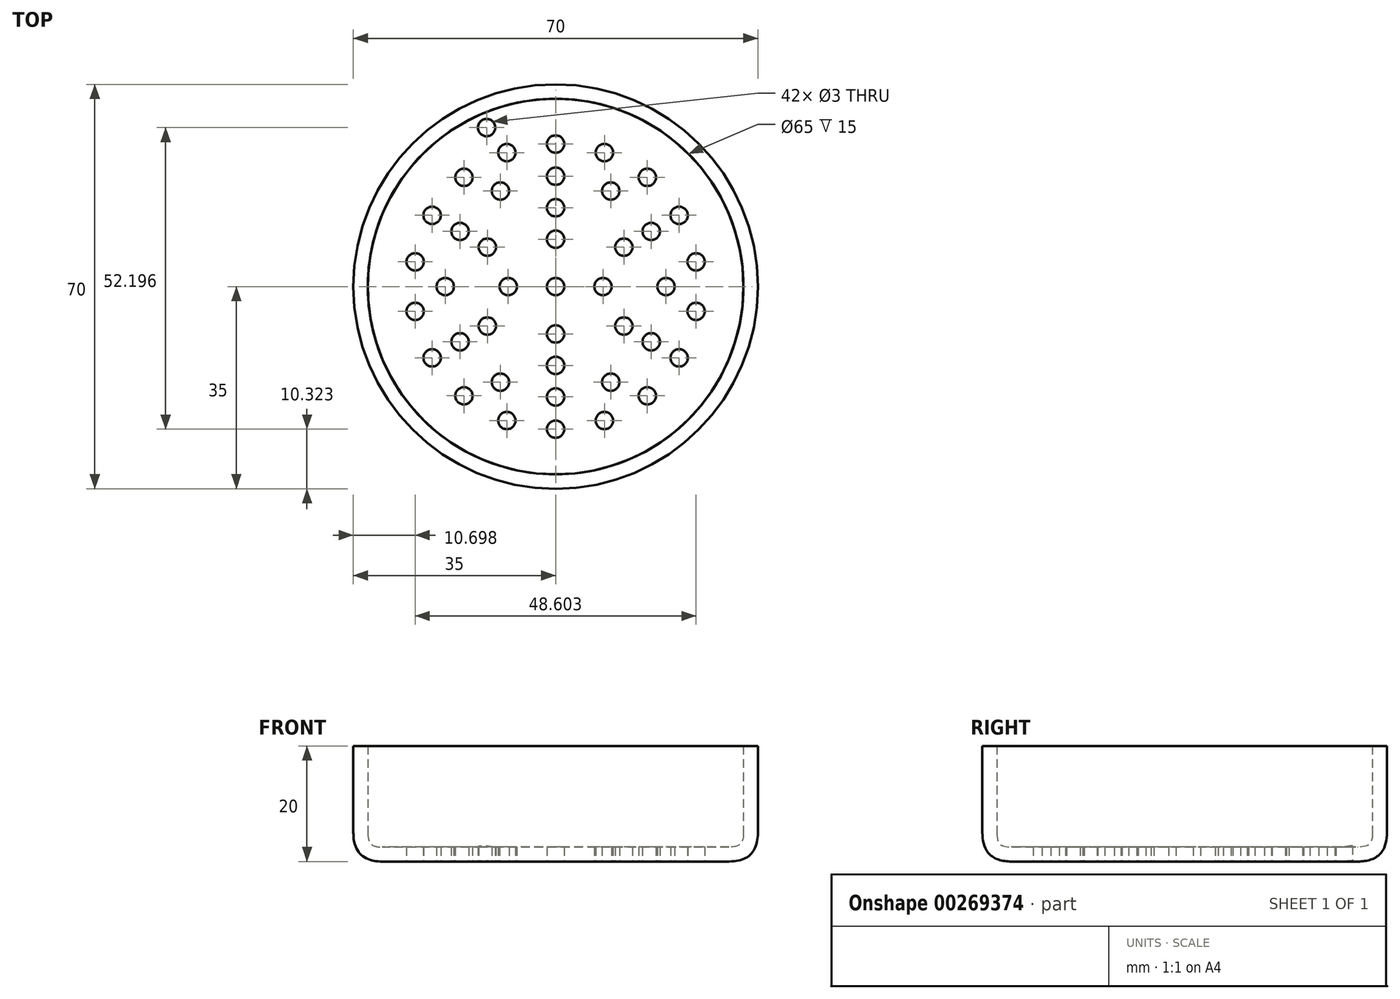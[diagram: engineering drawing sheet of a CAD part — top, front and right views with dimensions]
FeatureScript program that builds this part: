
annotation { "Feature Type Name" : "Feature", "Feature Type Description" : "" }
export const myFeature = defineFeature(function(context is Context, id is Id, definition is map)
    precondition{}
    {
        {
            var Q0;
            Q0=qCreatedBy(makeId("Top.planeOp"),FACE);
            var sketch = newSketch(context, id + "F0", { "sketchPlane" : qUnion([Q0])});
            skCircle(sketch, "E0", {"center": v(0, 0) * mm, "radius": 35 * mm});
            skSolve(sketch);
        }
        {
            var Q0;
            Q0=makeQuery(id+"F0.imprint","IMPRINT",FACE,{"disambiguationData":[TD([[makeQuery(id+"F0.imprint","IMPRINT",EDGE,{"derivedFrom":sQuery(id+"F0.wireOp",EDGE,"E0")}),1.0]])]});
            extrude(context, id + "F1", {"entities" : qUnion([Q0]), "depth" : 20 * mm});
        }
        {
            var Q0;
            Q0=makeQuery(id+"F1.opExtrude","CAP_EDGE",EDGE,{"disambiguationData":[OSD([sQuery(id+"F0.wireOp",EDGE,"E0")])],"isStart":true});
            fillet(context, id + "F2", {"entities" : qUnion([Q0]), "radius" : 5 * mm, "tangentPropagation" : true, "rho" : 0.5, "crossSection" : FilletCrossSection.CONIC, "allowEdgeOverflow" : false});
        }
        {
            var Q0;
            Q0=makeQuery(id+"F1.opExtrude","CAP_FACE",FACE,{"disambiguationData":[OSD([sQuery(id+"F0.wireOp",EDGE,"E0")])],"isStart":false});
            shell(context, id + "F3", {"entities" : qUnion([Q0]), "thickness" : 2.5 * mm});
        }
        {
            var Q0;
            Q0=makeQuery(id+"F1.opExtrude","CAP_FACE",FACE,{"disambiguationData":[OSD([sQuery(id+"F0.wireOp",EDGE,"E0")])],"isStart":true});
            var sketch = newSketch(context, id + "F4", { "sketchPlane" : qUnion([Q0])});
            skPoint(sketch, "E1", {"position": v(0, 0) * mm});
            skPoint(sketch, "E2", {"position": v(3.96, -29.74) * mm});
            skPoint(sketch, "E3", {"position": v(-11.94, -27.52) * mm});
            skPoint(sketch, "E4", {"position": v(0, -19.1) * mm});
            skPoint(sketch, "E5", {"position": v(-30, 0) * mm});
            skPoint(sketch, "E6", {"position": v(0, -8.2) * mm});
            skPoint(sketch, "E7", {"position": v(-33.56, -2.34) * mm});
            skPoint(sketch, "E8", {"position": v(-4.38, -20.96) * mm});
            skPoint(sketch, "E9", {"position": v(0, -13.64) * mm});
            skPoint(sketch, "E10", {"position": v(-12.69, -12.92) * mm});
            skPoint(sketch, "E11", {"position": v(0, -24.68) * mm});
            skPoint(sketch, "E12", {"position": v(-4.38, -46.93) * mm});
            skPoint(sketch, "E13.1.0", {"position": v(7.1, 4.1) * mm});
            skPoint(sketch, "E13.2.0", {"position": v(-7.1, 4.1) * mm});
            skPoint(sketch, "E14.1.0", {"position": v(8.2, 0) * mm});
            skPoint(sketch, "E14.2.0", {"position": v(0, 8.2) * mm});
            skPoint(sketch, "E14.3.0", {"position": v(-8.2, 0) * mm});
            skPoint(sketch, "E15.1.0", {"position": v(11.81, -6.82) * mm});
            skPoint(sketch, "E15.2.0", {"position": v(11.81, 6.82) * mm});
            skPoint(sketch, "E15.3.0", {"position": v(0, 13.64) * mm});
            skPoint(sketch, "E15.4.0", {"position": v(-11.81, 6.82) * mm});
            skPoint(sketch, "E15.5.0", {"position": v(-11.81, -6.82) * mm});
            skPoint(sketch, "E16.1.0", {"position": v(9.55, -16.54) * mm});
            skPoint(sketch, "E16.2.0", {"position": v(16.54, -9.55) * mm});
            skPoint(sketch, "E16.3.0", {"position": v(19.1, 0) * mm});
            skPoint(sketch, "E16.4.0", {"position": v(16.54, 9.55) * mm});
            skPoint(sketch, "E16.5.0", {"position": v(9.55, 16.54) * mm});
            skPoint(sketch, "E16.6.0", {"position": v(0, 19.1) * mm});
            skPoint(sketch, "E16.7.0", {"position": v(-9.55, 16.54) * mm});
            skPoint(sketch, "E16.8.0", {"position": v(-16.54, 9.55) * mm});
            skPoint(sketch, "E16.9.0", {"position": v(-19.1, 0) * mm});
            skPoint(sketch, "E16.10.0", {"position": v(-16.54, -9.55) * mm});
            skPoint(sketch, "E16.11.0", {"position": v(-9.55, -16.54) * mm});
            skPoint(sketch, "E17.1.0", {"position": v(8.44, -23.19) * mm});
            skPoint(sketch, "E17.2.0", {"position": v(15.86, -18.9) * mm});
            skPoint(sketch, "E17.3.0", {"position": v(21.37, -12.34) * mm});
            skPoint(sketch, "E17.4.0", {"position": v(24.3, -4.29) * mm});
            skPoint(sketch, "E17.5.0", {"position": v(24.3, 4.29) * mm});
            skPoint(sketch, "E17.6.0", {"position": v(21.37, 12.34) * mm});
            skPoint(sketch, "E17.7.0", {"position": v(15.86, 18.9) * mm});
            skPoint(sketch, "E17.8.0", {"position": v(8.44, 23.19) * mm});
            skPoint(sketch, "E17.9.0", {"position": v(0, 24.68) * mm});
            skPoint(sketch, "E17.10.0", {"position": v(-8.44, 23.19) * mm});
            skPoint(sketch, "E17.11.0", {"position": v(-15.86, 18.9) * mm});
            skPoint(sketch, "E17.12.0", {"position": v(-21.37, 12.34) * mm});
            skPoint(sketch, "E17.13.0", {"position": v(-24.3, 4.29) * mm});
            skPoint(sketch, "E17.14.0", {"position": v(-24.3, -4.29) * mm});
            skPoint(sketch, "E17.15.0", {"position": v(-21.37, -12.34) * mm});
            skPoint(sketch, "E17.16.0", {"position": v(-15.86, -18.9) * mm});
            skPoint(sketch, "E17.17.0", {"position": v(-8.44, -23.19) * mm});
            skSolve(sketch);
        }
        {
            var Q0;
            Q0=sQuery(id+"F4.wireOp",VERTEX,"E1");
            var Q1;
            Q1=sQuery(id+"F4.wireOp",VERTEX,"E6");
            var Q2;
            Q2=sQuery(id+"F4.wireOp",VERTEX,"E9");
            var Q3;
            Q3=sQuery(id+"F4.wireOp",VERTEX,"E4");
            var Q4;
            Q4=sQuery(id+"F4.wireOp",VERTEX,"E11");
            var Q5;
            Q5=sQuery(id+"F4.wireOp",VERTEX,"E14.3.0");
            var Q6;
            Q6=sQuery(id+"F4.wireOp",VERTEX,"E14.1.0");
            var Q7;
            Q7=sQuery(id+"F4.wireOp",VERTEX,"E14.2.0");
            var Q8;
            Q8=sQuery(id+"F4.wireOp",VERTEX,"E15.3.0");
            var Q9;
            Q9=sQuery(id+"F4.wireOp",VERTEX,"E16.6.0");
            var Q10;
            Q10=sQuery(id+"F4.wireOp",VERTEX,"E17.9.0");
            var Q11;
            Q11=sQuery(id+"F4.wireOp",VERTEX,"E17.8.0");
            var Q12;
            Q12=sQuery(id+"F4.wireOp",VERTEX,"E17.7.0");
            var Q13;
            Q13=sQuery(id+"F4.wireOp",VERTEX,"E17.6.0");
            var Q14;
            Q14=sQuery(id+"F4.wireOp",VERTEX,"E17.5.0");
            var Q15;
            Q15=sQuery(id+"F4.wireOp",VERTEX,"E17.4.0");
            var Q16;
            Q16=sQuery(id+"F4.wireOp",VERTEX,"E17.3.0");
            var Q17;
            Q17=sQuery(id+"F4.wireOp",VERTEX,"E17.2.0");
            var Q18;
            Q18=sQuery(id+"F4.wireOp",VERTEX,"E17.1.0");
            var Q19;
            Q19=sQuery(id+"F4.wireOp",VERTEX,"E3");
            var Q20;
            Q20=sQuery(id+"F4.wireOp",VERTEX,"E17.17.0");
            var Q21;
            Q21=sQuery(id+"F4.wireOp",VERTEX,"E17.16.0");
            var Q22;
            Q22=sQuery(id+"F4.wireOp",VERTEX,"E17.15.0");
            var Q23;
            Q23=sQuery(id+"F4.wireOp",VERTEX,"E17.14.0");
            var Q24;
            Q24=sQuery(id+"F4.wireOp",VERTEX,"E17.13.0");
            var Q25;
            Q25=sQuery(id+"F4.wireOp",VERTEX,"E17.12.0");
            var Q26;
            Q26=sQuery(id+"F4.wireOp",VERTEX,"E17.11.0");
            var Q27;
            Q27=sQuery(id+"F4.wireOp",VERTEX,"E17.10.0");
            var Q28;
            Q28=sQuery(id+"F4.wireOp",VERTEX,"E16.3.0");
            var Q29;
            Q29=sQuery(id+"F4.wireOp",VERTEX,"E16.4.0");
            var Q30;
            Q30=sQuery(id+"F4.wireOp",VERTEX,"E16.2.0");
            var Q31;
            Q31=sQuery(id+"F4.wireOp",VERTEX,"E16.1.0");
            var Q32;
            Q32=sQuery(id+"F4.wireOp",VERTEX,"E16.5.0");
            var Q33;
            Q33=sQuery(id+"F4.wireOp",VERTEX,"E16.7.0");
            var Q34;
            Q34=sQuery(id+"F4.wireOp",VERTEX,"E16.11.0");
            var Q35;
            Q35=sQuery(id+"F4.wireOp",VERTEX,"E16.9.0");
            var Q36;
            Q36=sQuery(id+"F4.wireOp",VERTEX,"E16.8.0");
            var Q37;
            Q37=sQuery(id+"F4.wireOp",VERTEX,"E16.10.0");
            var Q38;
            Q38=sQuery(id+"F4.wireOp",VERTEX,"E15.1.0");
            var Q39;
            Q39=sQuery(id+"F4.wireOp",VERTEX,"E15.2.0");
            var Q40;
            Q40=sQuery(id+"F4.wireOp",VERTEX,"E15.4.0");
            var Q41;
            Q41=sQuery(id+"F4.wireOp",VERTEX,"E15.5.0");
            var Q42;
            Q42=makeQuery(id+"F1.opExtrude","SWEPT_BODY",BODY,{"disambiguationData":[OSD([sQuery(id+"F0.wireOp",EDGE,"E0")])]});
            hole(context, id + "F5", {"style" : HoleStyle.SIMPLE, "endStyle" : HoleEndStyle.THROUGH, "holeDiameter" : 3 * mm, "tappedDepth" : 12 * mm, "tapClearance" : 3, "locations" : qUnion([Q0, Q1, Q2, Q3, Q4, Q5, Q6, Q7, Q8, Q9, Q10, Q11, Q12, Q13, Q14, Q15, Q16, Q17, Q18, Q19, Q20, Q21, Q22, Q23, Q24, Q25, Q26, Q27, Q28, Q29, Q30, Q31, Q32, Q33, Q34, Q35, Q36, Q37, Q38, Q39, Q40, Q41]), "scope" : qUnion([Q42])});
        }
    });
